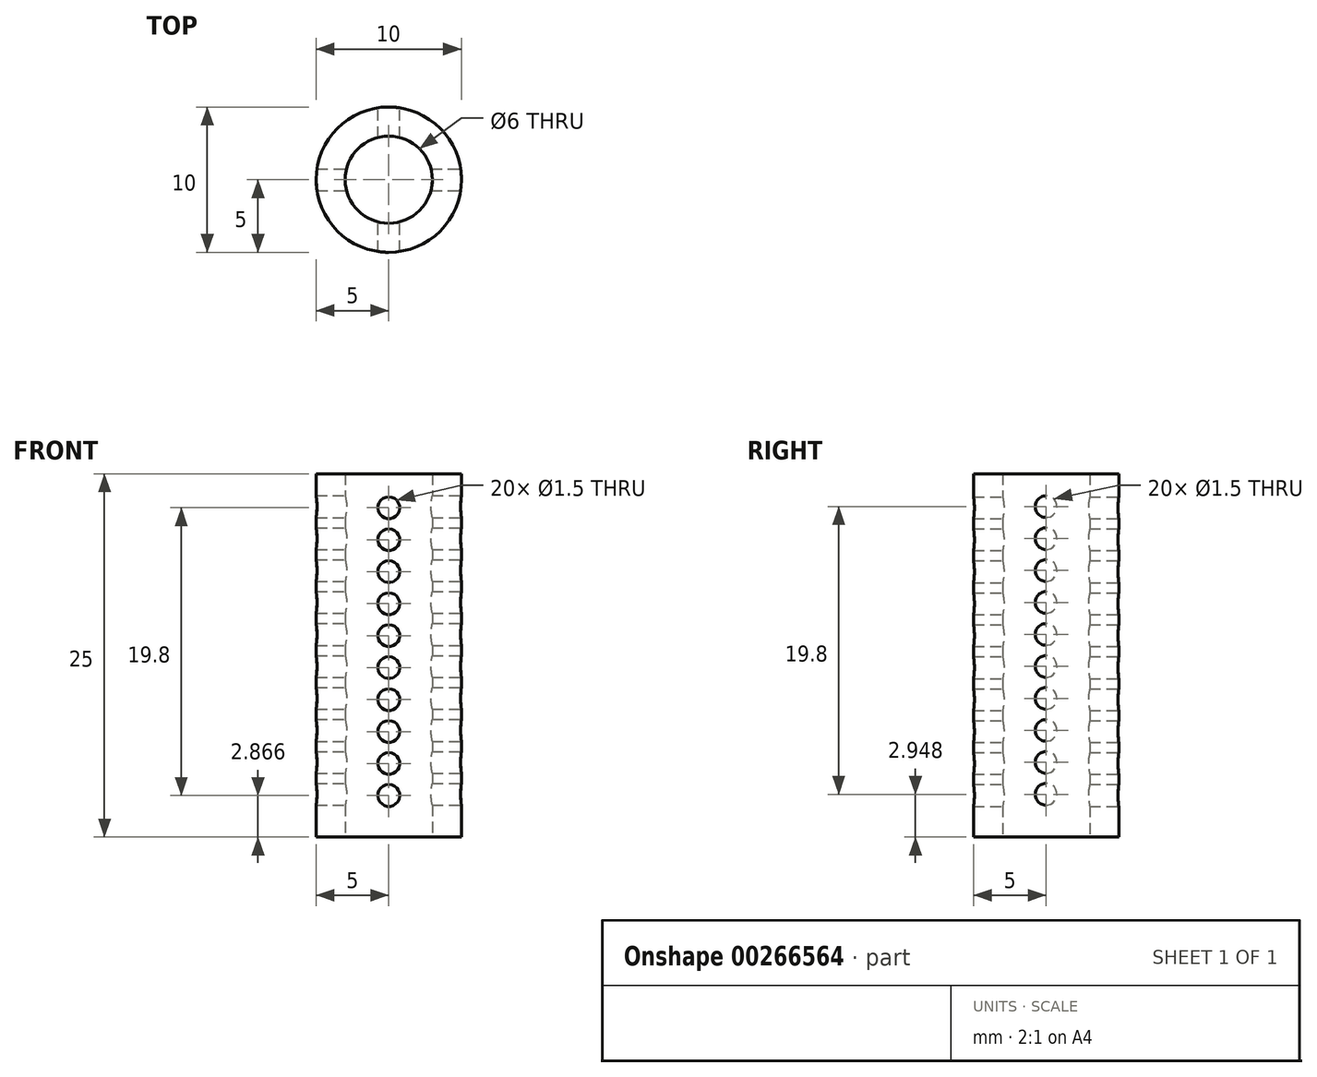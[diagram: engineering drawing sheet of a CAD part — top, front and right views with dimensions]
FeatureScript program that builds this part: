
annotation { "Feature Type Name" : "Feature", "Feature Type Description" : "" }
export const myFeature = defineFeature(function(context is Context, id is Id, definition is map)
    precondition{}
    {
        {
            var Q0;
            Q0=qCreatedBy(makeId("Top.planeOp"),FACE);
            var sketch = newSketch(context, id + "F0", { "sketchPlane" : qUnion([Q0])});
            skCircle(sketch, "E0", {"center": v(0, 0) * mm, "radius": 3 * mm});
            skCircle(sketch, "E1.0", {"center": v(0, 0) * mm, "radius": 5 * mm});
            skPoint(sketch, "E2", {"position": v(5, 0) * mm});
            skPoint(sketch, "E3", {"position": v(0, 5) * mm});
            skPoint(sketch, "E4", {"position": v(-5, 0) * mm});
            skPoint(sketch, "E5", {"position": v(0, -5) * mm});
            skSolve(sketch);
        }
        {
            var Q0;
            Q0 = qSketchRegion(id + "F0", true);
            extrude(context, id + "F1", {"entities" : qUnion([Q0]), "depth" : 25 * mm});
        }
        {
            var Q0;
            Q0=makeQuery(id+"F1.opExtrude","CAP_FACE",FACE,{"disambiguationData":[OSD([sQuery(id+"F0.wireOp",EDGE,"E0"),sQuery(id+"F0.wireOp",EDGE,"E1.0")])],"isStart":false});
            var sketch = newSketch(context, id + "F2", { "sketchPlane" : qUnion([Q0])});
            skPoint(sketch, "E6", {"position": v(5, 0) * mm});
            skPoint(sketch, "E7", {"position": v(-5, 0) * mm});
            skPoint(sketch, "E8", {"position": v(0, 5) * mm});
            skPoint(sketch, "E9", {"position": v(0, -5) * mm});
            skSolve(sketch);
        }
        {
            var Q0;
            Q0=qCreatedBy(makeId("Right.planeOp"),FACE);
            var Q1;
            Q1=sQuery(id+"F2.wireOp",VERTEX,"E6");
            cPlane(context, id + "F3", {"entities" : qUnion([Q0, Q1]), "cplaneType" : CPlaneType.PLANE_POINT, "offset" : 25 * mm, "width" : 150 * mm, "height" : 150 * mm});
        }
        {
            var Q0;
            Q0=qCreatedBy(id+"F3.planeOp",FACE);
            var sketch = newSketch(context, id + "F4", { "sketchPlane" : qUnion([Q0])});
            skCircle(sketch, "E10", {"center": v(0, 2.95) * mm, "radius": 0.75 * mm});
            skCircle(sketch, "E11.0.1.0", {"center": v(0, 5.15) * mm, "radius": 0.75 * mm});
            skCircle(sketch, "E11.0.2.0", {"center": v(0, 7.35) * mm, "radius": 0.75 * mm});
            skCircle(sketch, "E11.0.3.0", {"center": v(0, 9.55) * mm, "radius": 0.75 * mm});
            skCircle(sketch, "E11.0.4.0", {"center": v(0, 11.75) * mm, "radius": 0.75 * mm});
            skCircle(sketch, "E11.0.5.0", {"center": v(0, 13.95) * mm, "radius": 0.75 * mm});
            skCircle(sketch, "E11.0.6.0", {"center": v(0, 16.15) * mm, "radius": 0.75 * mm});
            skCircle(sketch, "E11.0.7.0", {"center": v(0, 18.35) * mm, "radius": 0.75 * mm});
            skCircle(sketch, "E11.0.8.0", {"center": v(0, 20.55) * mm, "radius": 0.75 * mm});
            skCircle(sketch, "E11.0.9.0", {"center": v(0, 22.75) * mm, "radius": 0.75 * mm});
            skLineSegment(sketch, "E11.direction1", {"start": v(0, 2.95) * mm, "end": v(25, 2.95) * mm, "construction": true});
            skLineSegment(sketch, "E11.direction2", {"start": v(0, 2.95) * mm, "end": v(0, 5.15) * mm, "construction": true});
            skSolve(sketch);
        }
        {
            var Q0;
            Q0 = qSketchRegion(id + "F4", true);
            extrude(context, id + "F5", {"entities" : qUnion([Q0]), "operationType" : NewBodyOperationType.REMOVE, "endBound" : BoundingType.THROUGH_ALL, "oppositeDirection" : true, "depth" : 25 * mm});
        }
        {
            var Q0;
            Q0=qCreatedBy(makeId("Front.planeOp"),FACE);
            var Q1;
            Q1=sQuery(id+"F2.wireOp",VERTEX,"E8");
            cPlane(context, id + "F6", {"entities" : qUnion([Q0, Q1]), "cplaneType" : CPlaneType.PLANE_POINT, "offset" : 25 * mm, "width" : 150 * mm, "height" : 150 * mm});
        }
        {
            var Q0;
            Q0=qCreatedBy(id+"F6.planeOp",FACE);
            var sketch = newSketch(context, id + "F7", { "sketchPlane" : qUnion([Q0])});
            skCircle(sketch, "E12", {"center": v(0, 2.87) * mm, "radius": 0.75 * mm});
            skCircle(sketch, "E13.0.1.0", {"center": v(0, 5.07) * mm, "radius": 0.75 * mm});
            skCircle(sketch, "E13.0.2.0", {"center": v(0, 7.27) * mm, "radius": 0.75 * mm});
            skCircle(sketch, "E13.0.3.0", {"center": v(0, 9.47) * mm, "radius": 0.75 * mm});
            skCircle(sketch, "E13.0.4.0", {"center": v(0, 11.67) * mm, "radius": 0.75 * mm});
            skCircle(sketch, "E13.0.5.0", {"center": v(0, 13.87) * mm, "radius": 0.75 * mm});
            skCircle(sketch, "E13.0.6.0", {"center": v(0, 16.07) * mm, "radius": 0.75 * mm});
            skCircle(sketch, "E13.0.7.0", {"center": v(0, 18.27) * mm, "radius": 0.75 * mm});
            skCircle(sketch, "E13.0.8.0", {"center": v(0, 20.47) * mm, "radius": 0.75 * mm});
            skCircle(sketch, "E13.0.9.0", {"center": v(0, 22.67) * mm, "radius": 0.75 * mm});
            skLineSegment(sketch, "E13.direction1", {"start": v(0, 2.87) * mm, "end": v(25, 2.87) * mm, "construction": true});
            skLineSegment(sketch, "E13.direction2", {"start": v(0, 2.87) * mm, "end": v(0, 5.07) * mm, "construction": true});
            skSolve(sketch);
        }
        {
            var Q0;
            Q0 = qSketchRegion(id + "F7", true);
            extrude(context, id + "F8", {"entities" : qUnion([Q0]), "operationType" : NewBodyOperationType.REMOVE, "endBound" : BoundingType.THROUGH_ALL, "depth" : 25 * mm});
        }
    });
